# Revit family: LOROWERK 01360-100X
name_source: partatom
category: Plumbing Fixtures
revit_build: Autodesk Revit 2017 (Build: 20160225_1515(x64)
units: mm (PartAtom-declared; Revit-internal decimal feet)

## family parameters
Always vertical = Yes
Cut with Voids When Loaded = No
Part Type = Normal
Room Calculation Point = No
Round Connector Dimension = Use Diameter
Shared = No
Work Plane-Based = No

## types (1)
- LOROWERK 01360-100X
    Abdichtvarianten = mit Klemmflansch (Pressdichtungsflansch)
    Abflussstutzen Ausführung = waagerecht
    Ablaufanschluss = seitlich
    Anschluss an GLT, GA = No
    BIM = https://media.stage.bim.site
    CONNECTOR0_DIAMETER_dZ_0r = 100 mm  [stored 0.328084 ft]
    CONNECTOR0_dZ_00 = 18 mm
    CONNECTOR0_dZ_01 = 18 mm
    CONNECTOR0_ref_dZ = 18 mm
    CONNECTOR1_DIAMETER_dNBN0_0r = 100 mm  [stored 0.328084 ft]
    CONNECTOR1_dNBN0_00 = 527 mm
    CONNECTOR1_dNBN0_01 = 601 mm
    CONNECTOR1_ref_dNBN0 = 527 mm
    CONNECTOR1_ref_dNBN1 = 13 mm
    DATANORM = 01360.100X
    Description = LORO-RAINSTAR Attikaabläufe, Serie 89, Eingrifftiefe 55 mm
    Einbaubreite [m] = 0.27
    Einbauhöhe [m] = 0.215
    Einbautiefe [m] = 0.738
    Elektrischer Anschluss = No
    Feuerwiderstandsklasse nachrüstbar 5 = No
    GTIN = 4038088074671
    Gehäuseanschlussarten = Ablauf-Punktförmig
    Geruchsverschluss = ohne Geruchverschluss
    HAN = 01360.100X
    Ist System = No
    Ist Zubehör = No
    Komplettartikel (Einteilig) aus Kombination (Mehrteileausführung) Ablaufgrundkörper und Aufsatzstück = Yes
    Manufacturer = LOROWERK K.H. Vahlbrauk GmbH & Co. KG
    Nenndrucksystem = PN
    Nennmaß = 100
    Nennweitensystem = DN
    Potenzialausgleich (Erdungsanschluss) vorhanden = No
    Produktbezeichnung = LORO-RAINSTAR Attikaabläufe, Serie 89, Eingrifftiefe 55 mm
    Produktklassifikation = Attikaablauf
    Produktname = LORO-RAINSTAR 89 Attikaablauf, Einbau 55mm, Edelst., Klemmfl., f. Bitumenbahn, Freispiegel, DN100
    Produktvideo = https://media.stage.bim.site
    Sperrwasserhöhe [m] = 0
    Typ = Attikaablauf
    Type Name = LORO-RAINSTAR 89 Attikaablauf, Einbau 55mm, Edelst., Klemmfl., f. Bitumenbahn, Freispiegel, DN100
    VDIBSN = 0020080000020010000010020010010000000030020000000200000001
    Variante/Varianten-Art/Zubehörbezeichnung = ohne Begleitheizung
    Werkstoff des Ablaufkörpers = nicht rostender Stahl
    mit Blätter-/Kiesfang = Yes
    mit Schallentkopplung = No

note: [stored X ft] marks values corroborated as IEEE doubles in the binary element streams (Revit-internal decimal feet)

## geometry (parser evidence)
native form markers: Blend x2, Sweep x3
no freeform markers — native parametric forms only
